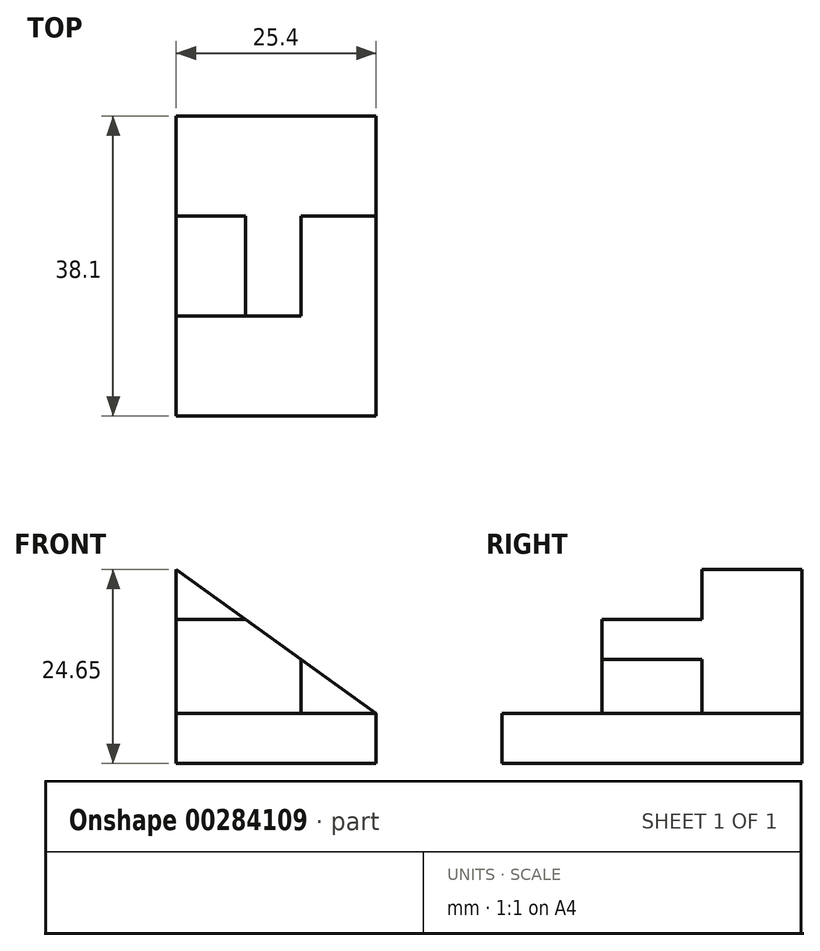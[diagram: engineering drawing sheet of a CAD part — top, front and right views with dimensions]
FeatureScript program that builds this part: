
annotation { "Feature Type Name" : "Feature", "Feature Type Description" : "" }
export const myFeature = defineFeature(function(context is Context, id is Id, definition is map)
    precondition{}
    {
        {
            var Q0;
            Q0=qCreatedBy(makeId("Front.planeOp"),FACE);
            var sketch = newSketch(context, id + "F0", { "sketchPlane" : qUnion([Q0])});
            skLineSegment(sketch, "E0.bottom", {"start": v(0, 0) * mm, "end": v(25.4, 0) * mm});
            skLineSegment(sketch, "E0.top", {"start": v(0, 6.35) * mm, "end": v(25.4, 6.35) * mm});
            skLineSegment(sketch, "E0.left", {"start": v(0, 0) * mm, "end": v(0, 6.35) * mm});
            skLineSegment(sketch, "E0.right", {"start": v(25.4, 0) * mm, "end": v(25.4, 6.35) * mm});
            skLineSegment(sketch, "E1", {"start": v(0, 6.35) * mm, "end": v(0, 24.65) * mm});
            skLineSegment(sketch, "E2", {"start": v(0, 24.65) * mm, "end": v(25.4, 6.35) * mm});
            skSolve(sketch);
        }
        {
            var Q0;
            Q0 = qSketchRegion(id + "F0", true);
            extrude(context, id + "F1", {"entities" : qUnion([Q0]), "depth" : 38.1 * mm});
        }
        {
            var Q0;
            Q0=makeQuery(id+"F1.opExtrude","CAP_FACE",FACE,{"disambiguationData":[OSD([sQuery(id+"F0.wireOp",EDGE,"E0.bottom"),sQuery(id+"F0.wireOp",EDGE,"E0.left"),sQuery(id+"F0.wireOp",EDGE,"E0.right"),sQuery(id+"F0.wireOp",EDGE,"E1"),sQuery(id+"F0.wireOp",EDGE,"E2")])],"isStart":false});
            var sketch = newSketch(context, id + "F2", { "sketchPlane" : qUnion([Q0])});
            skLineSegment(sketch, "E3", {"start": v(25.4, 6.35) * mm, "end": v(0, 6.35) * mm});
            skLineSegment(sketch, "E4", {"start": v(0, 6.35) * mm, "end": v(0, 24.65) * mm});
            skLineSegment(sketch, "E5", {"start": v(0, 24.65) * mm, "end": v(25.4, 6.35) * mm});
            skSolve(sketch);
        }
        {
            var Q0;
            Q0=makeQuery(id+"F2.imprint","IMPRINT",FACE,{"disambiguationData":[TD([[makeQuery(id+"F2.imprint","IMPRINT",EDGE,{"derivedFrom":sQuery(id+"F2.wireOp",EDGE,"E3")}),-1.0]])]});
            extrude(context, id + "F3", {"entities" : qUnion([Q0]), "operationType" : NewBodyOperationType.REMOVE, "oppositeDirection" : true, "depth" : 12.7 * mm});
        }
        {
            var Q0;
            Q0=makeQuery(id+"F3.boolean.opBoolean","COPY",FACE,{"derivedFrom":makeQuery(id+"F3.opExtrude","CAP_FACE",FACE,{"disambiguationData":[OSD([sQuery(id+"F2.wireOp",EDGE,"E3"),sQuery(id+"F2.wireOp",EDGE,"E4"),sQuery(id+"F2.wireOp",EDGE,"E5")])],"isStart":false})});
            var sketch = newSketch(context, id + "F4", { "sketchPlane" : qUnion([Q0])});
            skLineSegment(sketch, "E6", {"start": v(0, 24.65) * mm, "end": v(0, 18.3) * mm});
            skLineSegment(sketch, "E7", {"start": v(0, 18.3) * mm, "end": v(8.81, 18.3) * mm});
            skLineSegment(sketch, "E8", {"start": v(8.81, 18.3) * mm, "end": v(0, 24.65) * mm});
            skSolve(sketch);
        }
        {
            var Q0;
            Q0 = qSketchRegion(id + "F4", true);
            extrude(context, id + "F5", {"entities" : qUnion([Q0]), "operationType" : NewBodyOperationType.REMOVE, "oppositeDirection" : true, "depth" : 12.7 * mm});
        }
        {
            var Q0;
            Q0=makeQuery(id+"F3.boolean.opBoolean","COPY",FACE,{"derivedFrom":makeQuery(id+"F3.opExtrude","CAP_FACE",FACE,{"disambiguationData":[OSD([sQuery(id+"F2.wireOp",EDGE,"E3"),sQuery(id+"F2.wireOp",EDGE,"E4"),sQuery(id+"F2.wireOp",EDGE,"E5")])],"isStart":false})});
            var sketch = newSketch(context, id + "F6", { "sketchPlane" : qUnion([Q0])});
            skLineSegment(sketch, "E9", {"start": v(25.4, 6.35) * mm, "end": v(15.88, 6.35) * mm});
            skLineSegment(sketch, "E10", {"start": v(15.88, 6.35) * mm, "end": v(15.88, 13.21) * mm});
            skLineSegment(sketch, "E11", {"start": v(15.88, 13.21) * mm, "end": v(25.4, 6.35) * mm});
            skSolve(sketch);
        }
        {
            var Q0;
            Q0 = qSketchRegion(id + "F6", true);
            extrude(context, id + "F7", {"entities" : qUnion([Q0]), "operationType" : NewBodyOperationType.REMOVE, "oppositeDirection" : true, "depth" : 12.7 * mm});
        }
    });
